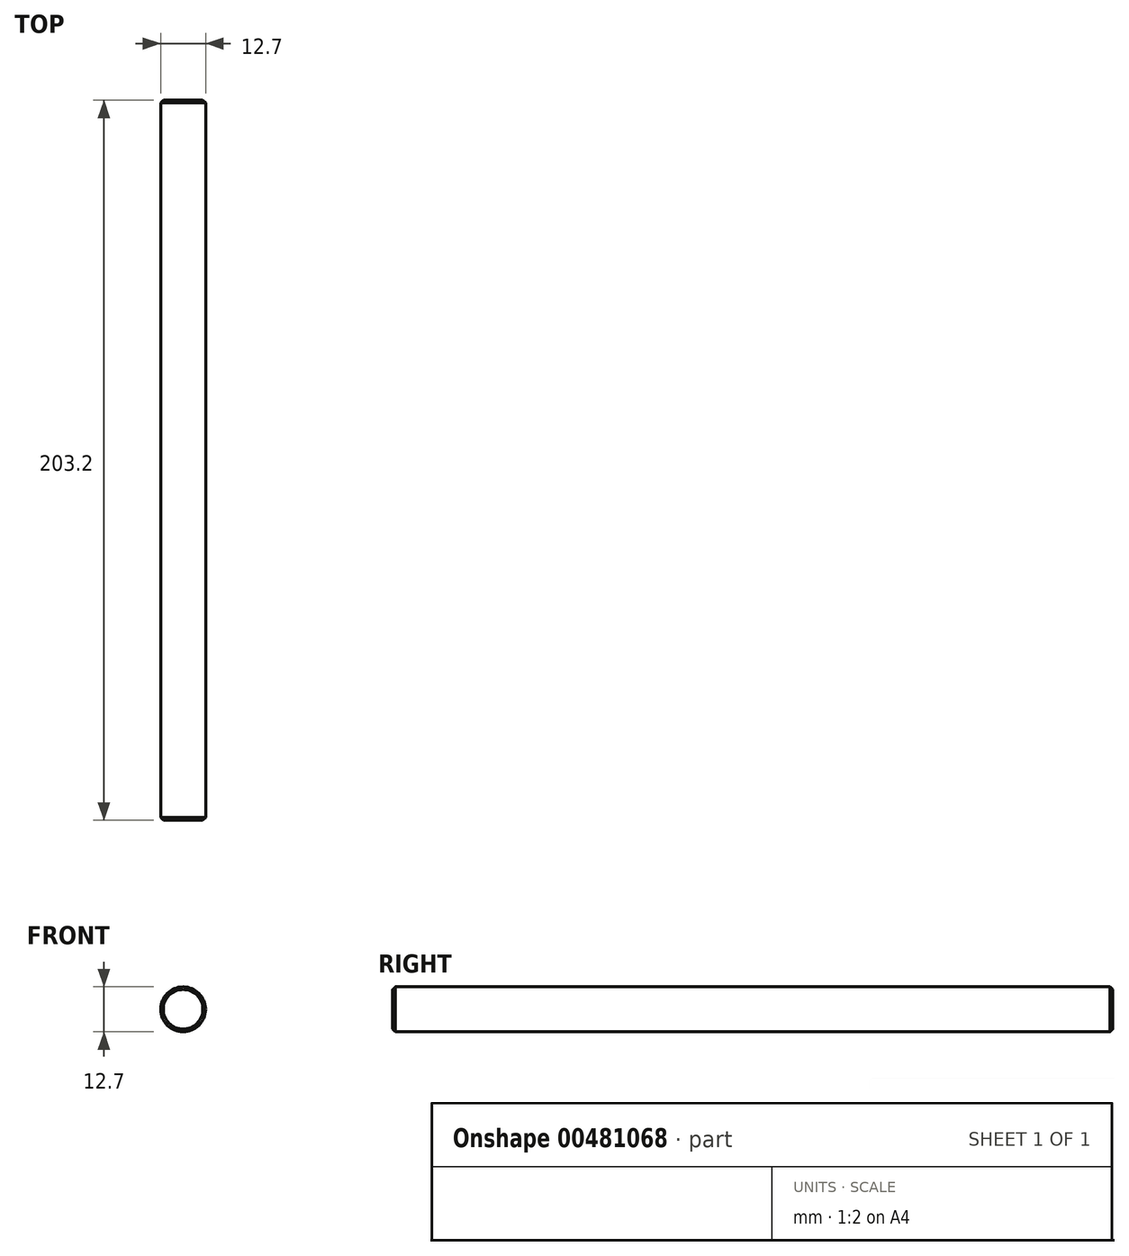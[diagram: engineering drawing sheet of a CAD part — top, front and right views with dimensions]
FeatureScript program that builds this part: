
annotation { "Feature Type Name" : "Feature", "Feature Type Description" : "" }
export const myFeature = defineFeature(function(context is Context, id is Id, definition is map)
    precondition{}
    {
        {
            var Q0;
            Q0=qCreatedBy(makeId("Right.planeOp"),FACE);
            var sketch = newSketch(context, id + "F0", { "sketchPlane" : qUnion([Q0])});
            skLineSegment(sketch, "E0", {"start": v(0, 0) * mm, "end": v(-203.2, 0) * mm});
            skLineSegment(sketch, "E1", {"start": v(-203.2, 0) * mm, "end": v(-203.2, 6.35) * mm});
            skLineSegment(sketch, "E2", {"start": v(-203.2, 6.35) * mm, "end": v(0, 6.35) * mm});
            skLineSegment(sketch, "E3", {"start": v(0, 6.35) * mm, "end": v(0, 0) * mm});
            skSolve(sketch);
        }
        {
            var Q0;
            Q0=makeQuery(id+"F0.imprint","IMPRINT",FACE,{"disambiguationData":[TD([[makeQuery(id+"F0.imprint","IMPRINT",EDGE,{"derivedFrom":sQuery(id+"F0.wireOp",EDGE,"E0")}),-1.0]])]});
            var Q1;
            Q1=sQuery(id+"F0.wireOp",EDGE,"E0");
            revolve(context, id + "F1", {"entities" : qUnion([Q0]), "axis" : qUnion([Q1]), "revolveType" : RevolveType.FULL});
        }
        {
            var Q0;
            Q0=makeQuery(id+"F1.opRevolve","SWEPT_EDGE",EDGE,{"disambiguationData":[OSD([sQuery(id+"F0.wireOp",EDGE,"E1"),sQuery(id+"F0.wireOp",EDGE,"E2")])]});
            var Q1;
            Q1=makeQuery(id+"F1.opRevolve","SWEPT_EDGE",EDGE,{"disambiguationData":[OSD([sQuery(id+"F0.wireOp",EDGE,"E2"),sQuery(id+"F0.wireOp",EDGE,"E3")])]});
            chamfer(context, id + "F2", {"entities" : qUnion([Q0, Q1]), "width" : 0.76 * mm, "tangentPropagation" : true});
        }
    });
